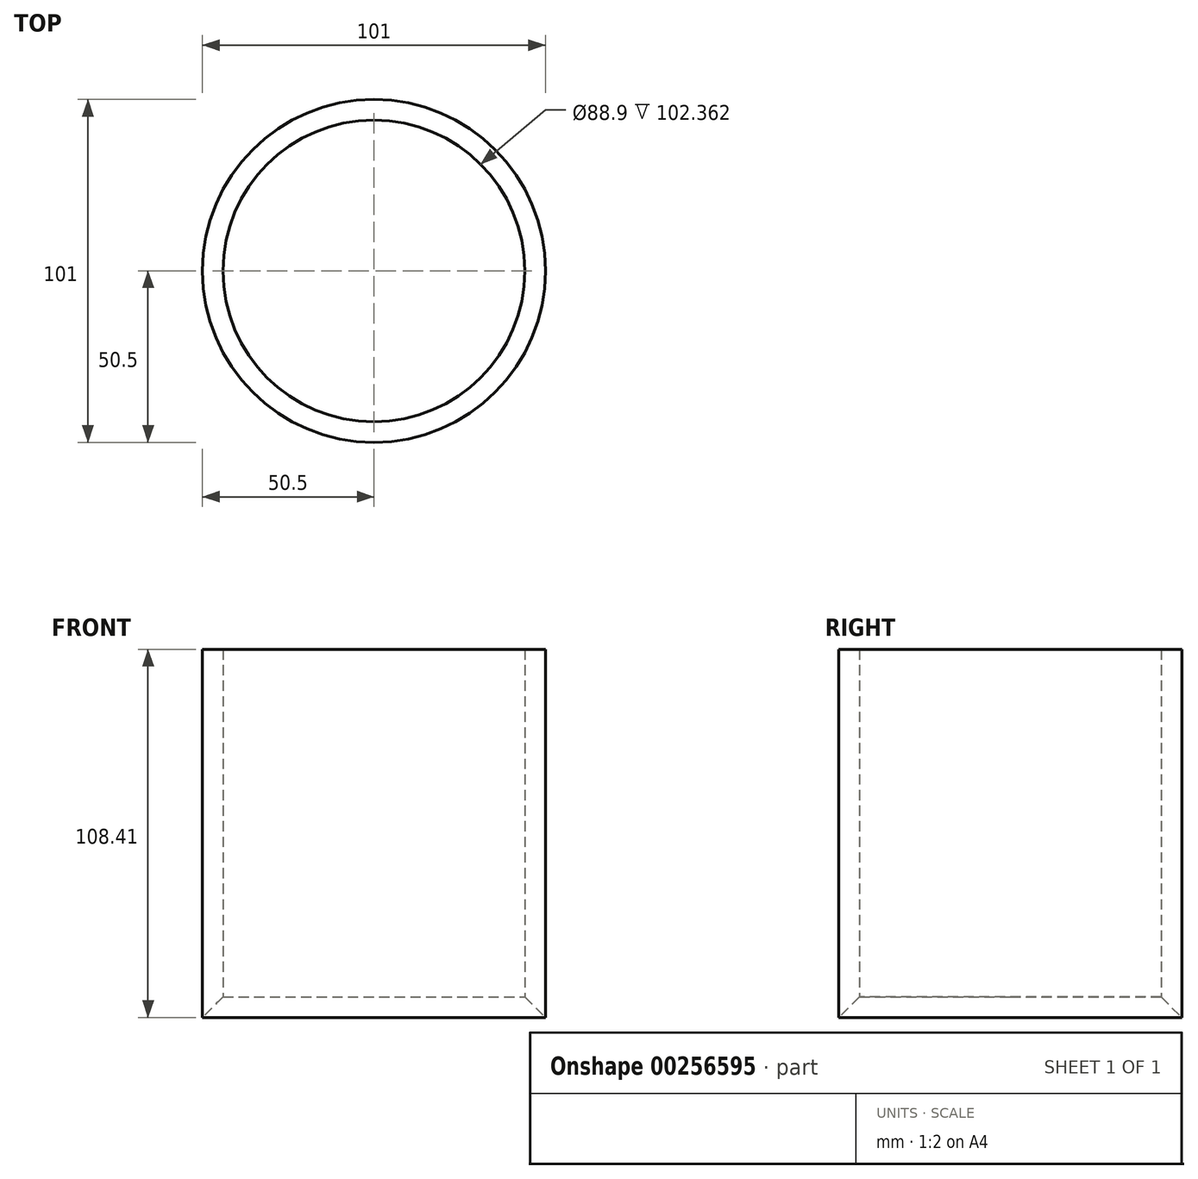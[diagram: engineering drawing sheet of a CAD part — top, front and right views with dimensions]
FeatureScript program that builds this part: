
annotation { "Feature Type Name" : "Feature", "Feature Type Description" : "" }
export const myFeature = defineFeature(function(context is Context, id is Id, definition is map)
    precondition{}
    {
        {
            var Q0;
            Q0=qCreatedBy(makeId("Top.planeOp"),FACE);
            var sketch = newSketch(context, id + "F0", { "sketchPlane" : qUnion([Q0])});
            skCircle(sketch, "E0", {"center": v(0, 0) * mm, "radius": 50.5 * mm});
            skSolve(sketch);
        }
        {
            var Q0;
            Q0=makeQuery(id+"F0.imprint","IMPRINT",FACE,{"disambiguationData":[TD([[makeQuery(id+"F0.imprint","IMPRINT",EDGE,{"derivedFrom":sQuery(id+"F0.wireOp",EDGE,"E0")}),1.0]])]});
            extrude(context, id + "F1", {"entities" : qUnion([Q0]), "depth" : 108.7 * mm});
        }
        {
            var Q0;
            Q0=qCreatedBy(makeId("Top.planeOp"),FACE);
            var sketch = newSketch(context, id + "F2", { "sketchPlane" : qUnion([Q0])});
            skCircle(sketch, "E1", {"center": v(0, 0) * mm, "radius": 34.92 * mm});
            skSolve(sketch);
        }
        {
            var Q0;
            Q0=sQuery(id+"F2.wireOp",VERTEX,"E1.center");
            var Q1;
            Q1=makeQuery(id+"F1.opExtrude","SWEPT_BODY",BODY,{"disambiguationData":[OSD([sQuery(id+"F0.wireOp",EDGE,"E0")])]});
            hole(context, id + "F3", {"style" : HoleStyle.C_SINK, "endStyle" : HoleEndStyle.THROUGH, "oppositeDirection" : true, "holeDiameter" : 88.9 * mm, "cSinkDiameter" : 101.6 * mm, "cSinkAngle" : 90 * degree, "tappedDepth" : 12.7 * mm, "tapClearance" : 3, "startFromSketch" : true, "locations" : qUnion([Q0]), "scope" : qUnion([Q1])});
        }
    });
